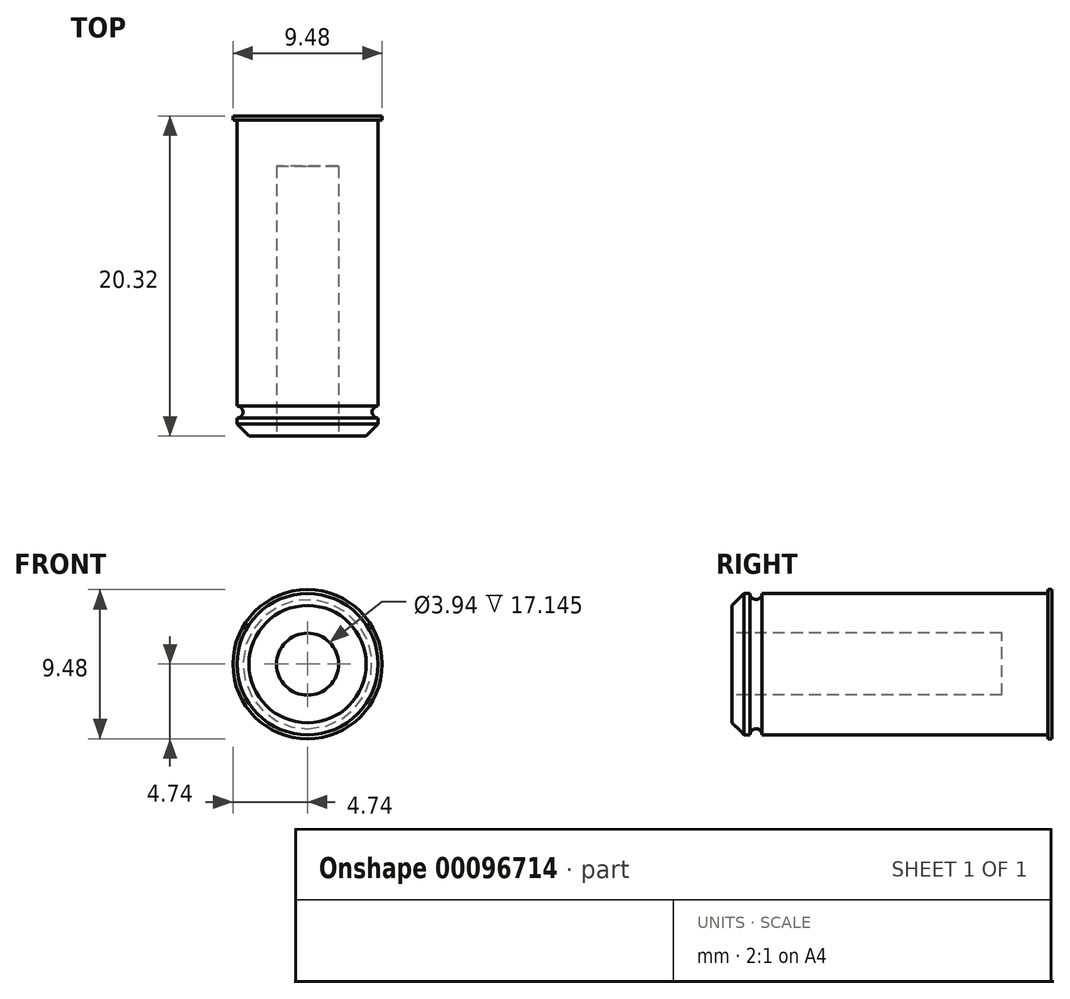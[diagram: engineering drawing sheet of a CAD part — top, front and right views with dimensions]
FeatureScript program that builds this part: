
annotation { "Feature Type Name" : "Feature", "Feature Type Description" : "" }
export const myFeature = defineFeature(function(context is Context, id is Id, definition is map)
    precondition{}
    {
        {
            var Q0;
            Q0=qCreatedBy(makeId("Right.planeOp"),FACE);
            var sketch = newSketch(context, id + "F0", { "sketchPlane" : qUnion([Q0])});
            skLineSegment(sketch, "E0", {"start": v(0.76, 4.48) * mm, "end": v(1.14, 4.48) * mm});
            skLineSegment(sketch, "E1", {"start": v(20.32, 4.48) * mm, "end": v(20.32, 0) * mm});
            skLineSegment(sketch, "E2", {"start": v(0, 3.72) * mm, "end": v(0, 1.97) * mm});
            skLineSegment(sketch, "E3", {"start": v(0, 1.97) * mm, "end": v(17.15, 1.97) * mm});
            skLineSegment(sketch, "E4", {"start": v(17.15, 1.97) * mm, "end": v(17.15, 0) * mm});
            skLineSegment(sketch, "E5", {"start": v(17.15, 0) * mm, "end": v(20.32, 0) * mm});
            skLineSegment(sketch, "E6", {"start": v(0, 3.72) * mm, "end": v(0.76, 4.48) * mm});
            skArc(sketch, "E7", {"start": v(1.14, 4.48) * mm, "mid": v(1.52, 4.1) * mm, "end": v(1.9, 4.48) * mm});
            skLineSegment(sketch, "E8.trimOffspring", {"start": v(1.9, 4.48) * mm, "end": v(20.07, 4.48) * mm});
            skLineSegment(sketch, "E9", {"start": v(20.32, 4.48) * mm, "end": v(20.32, 4.74) * mm});
            skLineSegment(sketch, "E10", {"start": v(20.32, 4.74) * mm, "end": v(20.07, 4.74) * mm});
            skLineSegment(sketch, "E11", {"start": v(20.07, 4.74) * mm, "end": v(20.07, 4.48) * mm});
            skSolve(sketch);
        }
        {
            var Q0;
            Q0=qCreatedBy(makeId("Right.planeOp"),FACE);
            var sketch = newSketch(context, id + "F1", { "sketchPlane" : qUnion([Q0])});
            skLineSegment(sketch, "E12", {"start": v(0, 0) * mm, "end": v(8.38, 0) * mm, "construction": true});
            skSolve(sketch);
        }
        {
            var Q0;
            Q0 = qSketchRegion(id + "F0", true);
            var Q1;
            Q1=sQuery(id+"F1.wireOp",EDGE,"E12");
            revolve(context, id + "F2", {"entities" : qUnion([Q0]), "axis" : qUnion([Q1]), "revolveType" : RevolveType.FULL});
        }
    });
